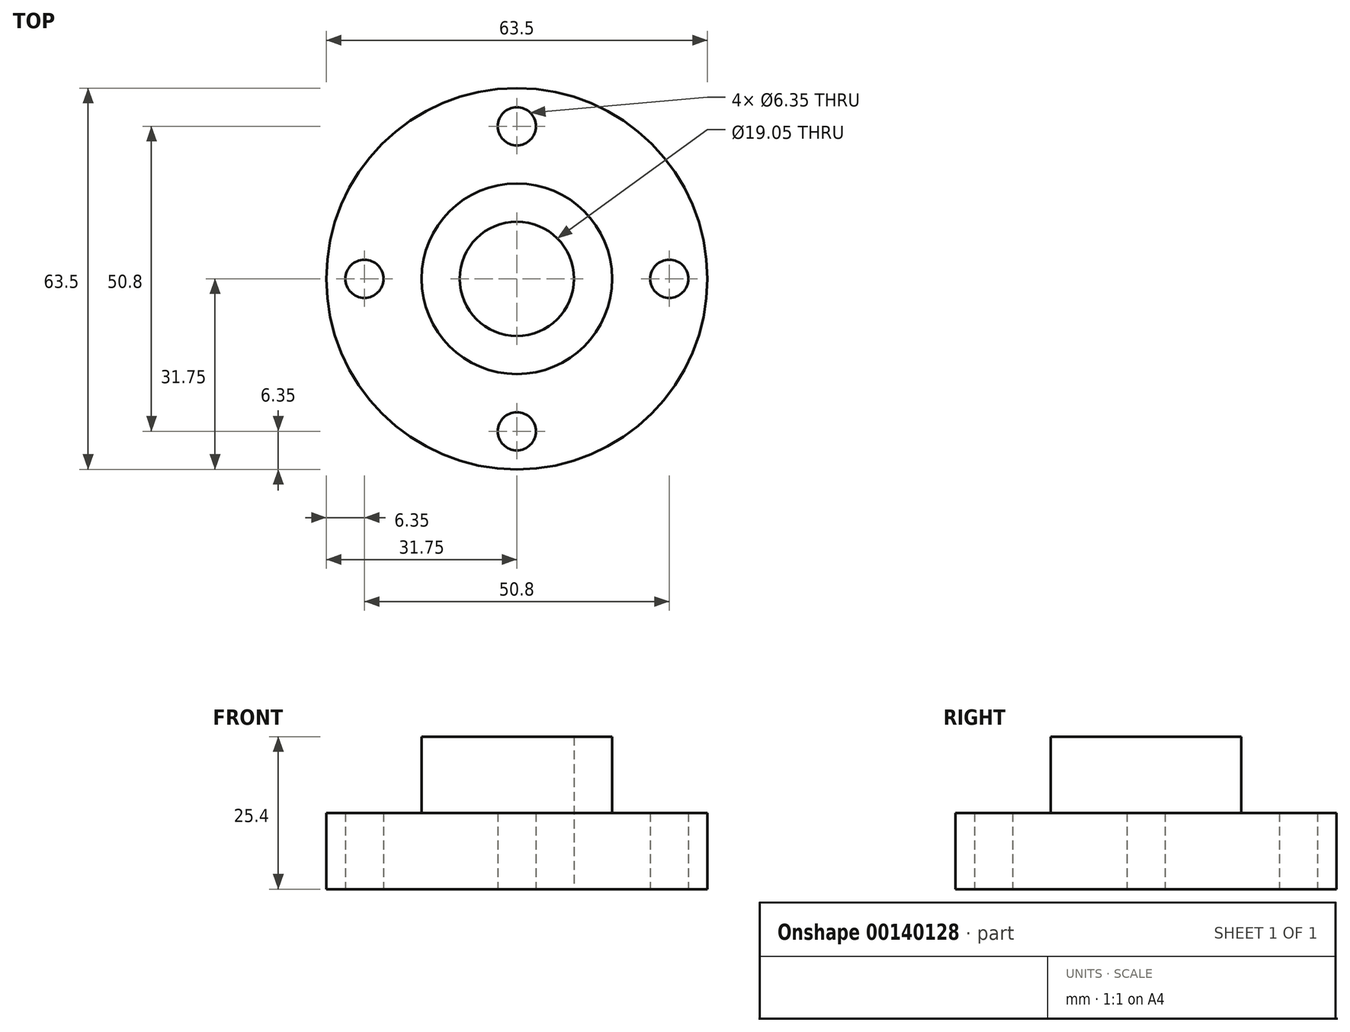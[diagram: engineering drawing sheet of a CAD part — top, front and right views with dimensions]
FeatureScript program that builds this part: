
annotation { "Feature Type Name" : "Feature", "Feature Type Description" : "" }
export const myFeature = defineFeature(function(context is Context, id is Id, definition is map)
    precondition{}
    {
        {
            var Q0;
            Q0=qCreatedBy(makeId("Top.planeOp"),FACE);
            var sketch = newSketch(context, id + "F0", { "sketchPlane" : qUnion([Q0])});
            skCircle(sketch, "E0", {"center": v(0, 0) * mm, "radius": 9.53 * mm});
            skCircle(sketch, "E1", {"center": v(0, 0) * mm, "radius": 15.88 * mm});
            skCircle(sketch, "E2", {"center": v(0, 0) * mm, "radius": 31.75 * mm});
            skLineSegment(sketch, "E3", {"start": v(0, 0) * mm, "end": v(25.4, 0) * mm, "construction": true});
            skLineSegment(sketch, "E4", {"start": v(0, 0) * mm, "end": v(0, 25.4) * mm, "construction": true});
            skLineSegment(sketch, "E5", {"start": v(0, 0) * mm, "end": v(-25.4, 0) * mm, "construction": true});
            skLineSegment(sketch, "E6", {"start": v(0, 0) * mm, "end": v(0, -25.4) * mm, "construction": true});
            skPoint(sketch, "E7", {"position": v(-25.4, 0) * mm});
            skPoint(sketch, "E8", {"position": v(0, 25.4) * mm});
            skPoint(sketch, "E9", {"position": v(25.4, 0) * mm});
            skPoint(sketch, "E10", {"position": v(0, -25.4) * mm});
            skSolve(sketch);
        }
        {
            var Q0;
            Q0=makeQuery(id+"F0.imprint","IMPRINT",FACE,{"disambiguationData":[TD([[makeQuery(id+"F0.imprint","IMPRINT",EDGE,{"derivedFrom":sQuery(id+"F0.wireOp",EDGE,"E1")}),-1.0]])]});
            extrude(context, id + "F1", {"entities" : qUnion([Q0]), "depth" : 12.7 * mm});
        }
        {
            var Q0;
            Q0=makeQuery(id+"F0.imprint","IMPRINT",FACE,{"disambiguationData":[TD([[makeQuery(id+"F0.imprint","IMPRINT",EDGE,{"derivedFrom":sQuery(id+"F0.wireOp",EDGE,"E0")}),-1.0]])]});
            extrude(context, id + "F2", {"entities" : qUnion([Q0]), "operationType" : NewBodyOperationType.ADD, "depth" : 25.4 * mm});
        }
        {
            var Q0;
            Q0=sQuery(id+"F0.wireOp",VERTEX,"E8");
            var Q1;
            Q1=sQuery(id+"F0.wireOp",VERTEX,"E7");
            var Q2;
            Q2=sQuery(id+"F0.wireOp",VERTEX,"E10");
            var Q3;
            Q3=sQuery(id+"F0.wireOp",VERTEX,"E9");
            var Q4;
            Q4=makeQuery(id+"F1.opExtrude","SWEPT_BODY",BODY,{"disambiguationData":[OSD([sQuery(id+"F0.wireOp",EDGE,"E1"),sQuery(id+"F0.wireOp",EDGE,"E2")])]});
            hole(context, id + "F3", {"style" : HoleStyle.SIMPLE, "endStyle" : HoleEndStyle.THROUGH, "oppositeDirection" : true, "holeDiameter" : 6.35 * mm, "locations" : qUnion([Q0, Q1, Q2, Q3]), "scope" : qUnion([Q4]), "isTappedThrough" : true});
        }
    });
